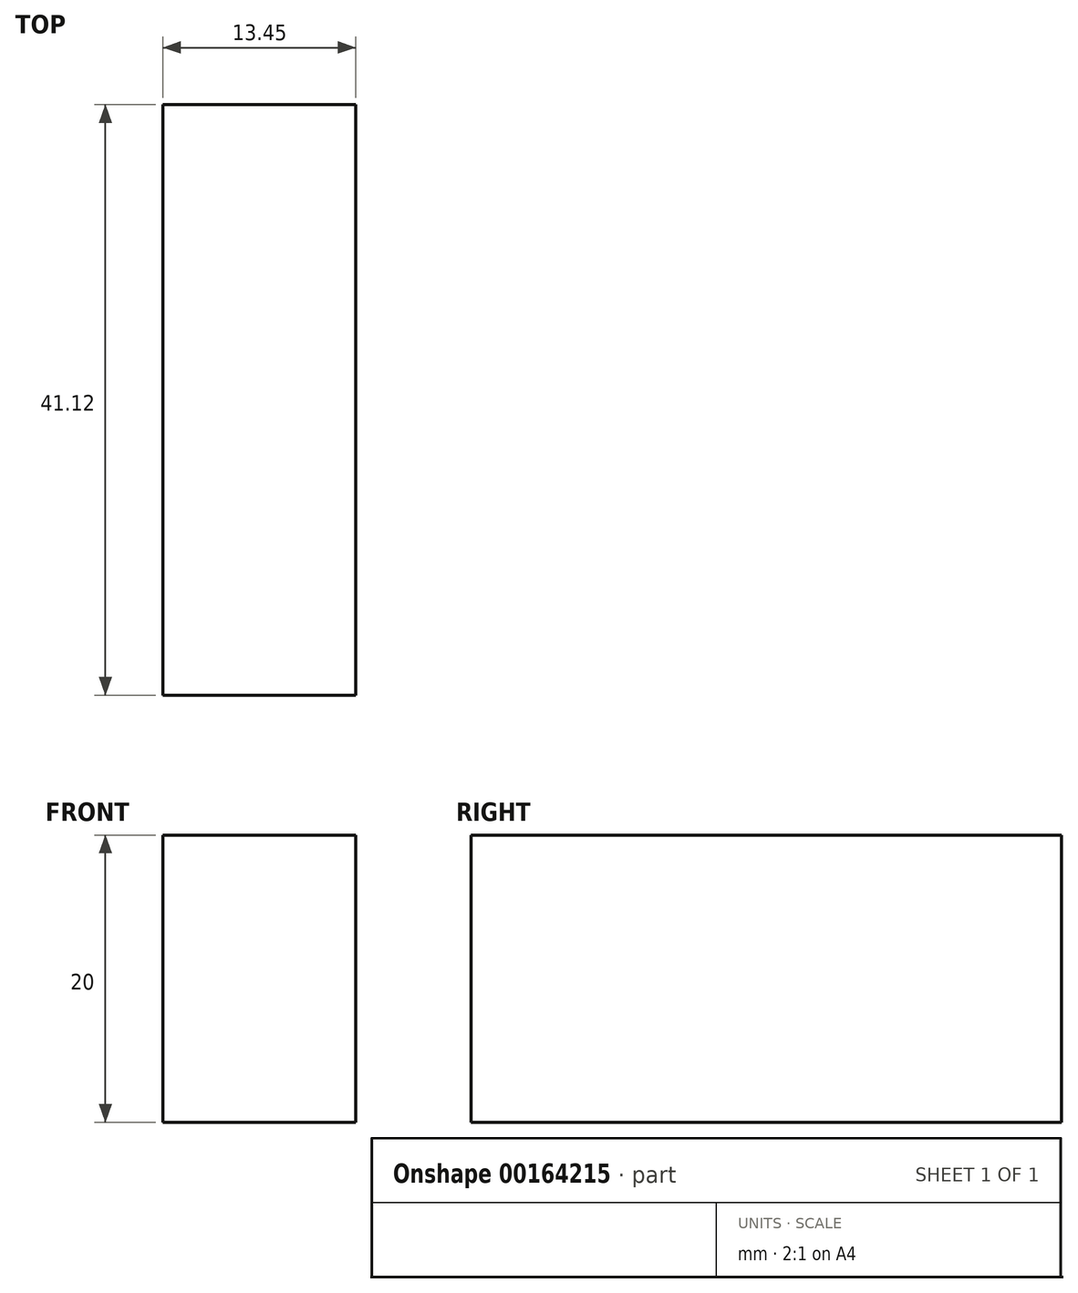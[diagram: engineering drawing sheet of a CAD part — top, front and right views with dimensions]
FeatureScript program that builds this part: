
annotation { "Feature Type Name" : "Feature", "Feature Type Description" : "" }
export const myFeature = defineFeature(function(context is Context, id is Id, definition is map)
    precondition{}
    {
        {
            var Q0;
            Q0=qCreatedBy(makeId("Top.planeOp"),FACE);
            cPlane(context, id + "F2", {"entities" : qUnion([Q0]), "cplaneType" : CPlaneType.OFFSET, "offset" : 25.4 * mm, "width" : 152.4 * mm, "height" : 152.4 * mm});
        }
        {
            var Q0;
            Q0=qCreatedBy(id+"F2.planeOp",FACE);
            var sketch = newSketch(context, id + "F0", { "sketchPlane" : qUnion([Q0])});
            skLineSegment(sketch, "E0.bottom", {"start": v(0, 24.62) * mm, "end": v(-13.45, 24.62) * mm});
            skLineSegment(sketch, "E0.top", {"start": v(0, -16.5) * mm, "end": v(-13.45, -16.5) * mm});
            skLineSegment(sketch, "E0.left", {"start": v(0, 24.62) * mm, "end": v(0, -16.5) * mm});
            skLineSegment(sketch, "E0.right", {"start": v(-13.45, 24.62) * mm, "end": v(-13.45, -16.5) * mm});
            skSolve(sketch);
        }
        {
            var Q0;
            Q0 = qSketchRegion(id + "F0", true);
            extrude(context, id + "F3", {"entities" : qUnion([Q0]), "depth" : 20 * mm});
        }
    });
